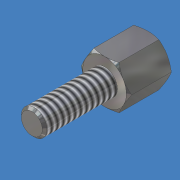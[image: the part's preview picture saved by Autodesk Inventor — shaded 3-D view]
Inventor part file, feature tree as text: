
AUTODESK INVENTOR PART (.ipt)
format: ipt  version: unknown  size: 220,160 bytes
history: native  units: mm (DEFAULTED — no unit token found)
features: sketch x4, extrude x2, chamfer x2, revolve x1, mirror x1, thread x1, hole x1
ambient origin geometry x8: Origin, YZ Plane, XZ Plane, XY Plane, X Axis, Y Axis, Z Axis, Center Point
feature tree (12):
  extrude  "Extrusion1"  Depth=4.7498mm TaperAngle=0.0deg
  revolve  "Revolution1"  [1 undecoded]
  mirror  "Mirror1"
  extrude  "Extrusion2"  Depth=25.4mm TaperAngle=0.0deg
  chamfer  "Chamfer1"  Angle=60.0deg  [1 undecoded]
  thread  "Thread1"  [1 undecoded]
  hole  "Hole1"  [1 undecoded]
  chamfer  "Chamfer2"  [1 undecoded]
  sketch  "Sketch1"  dims[d0=4.7498mm d1=4.7498mm d2=0.0mm]
  sketch  "Sketch2"  dims[d3=2.794mm d4=7.9375mm d5=0.0mm]
  sketch  "Sketch3"  dims[d6=0.254mm d7=3.175mm d8=25.4mm d9=0.0mm]
  sketch  "Sketch4"  dims[d11=90.0deg d12=60.0deg d13=2.159mm d14=5.08mm d15=9.525mm d16=6.35mm d17=14.3117mm d18=6.35mm d19=20.594885mm d20=0.254mm d21=3.175mm d22=45.0deg d23=45.0deg]
note: 5 required parameter values undecoded (feature->parameter linkage not recoverable at this tier; creation-order binding heuristic only, values carry confidence <= 0.55)